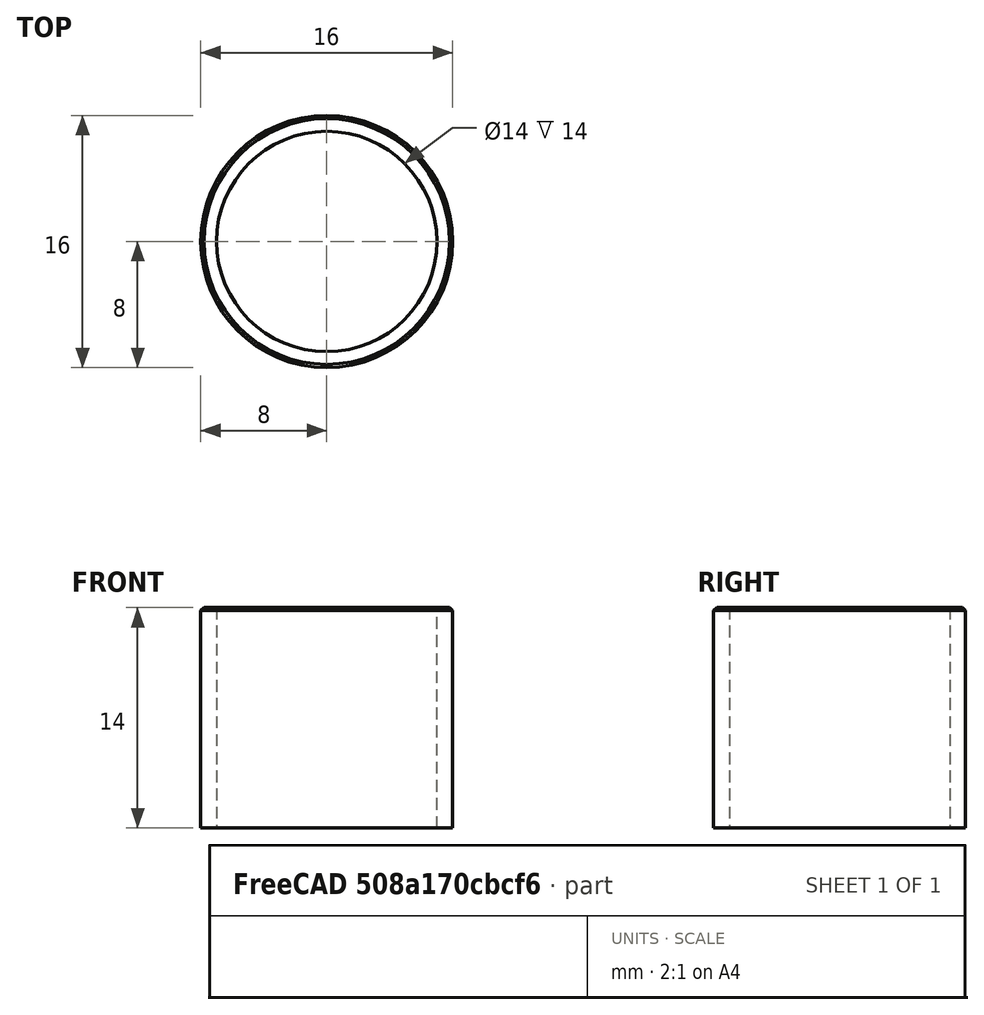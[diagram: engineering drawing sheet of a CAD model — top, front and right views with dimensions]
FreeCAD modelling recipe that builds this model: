
FCSTD DOCUMENT  (FreeCAD 0.19R24276 (Git))
Label: Roller_20_20_in_part_for_Bearing_5x16x5
License: All rights reserved
LicenseURL: http://en.wikipedia.org/wiki/All_rights_reserved
objects: Sketcher::SketchObject×1, PartDesign::Pad×1, PartDesign::Chamfer×1, PartDesign::Body×1
note: 6 computed .brp shape members not serialized (recipe doc carries the construction recipe); baked Part::Feature solids carry a one-line shape summary decoded from their .brp

FEATURE [Sketcher::SketchObject] Sketch
  FullyConstrained = true
  MapMode = 5
  Support = -> [XY_Plane]
  sketch-geometry (2):
    g0: Circle CenterX=0 CenterY=0 CenterZ=0 NormalX=0 NormalY=0 NormalZ=1 AngleXU=0 Radius=8
    g1: Circle CenterX=0 CenterY=0 CenterZ=0 NormalX=0 NormalY=0 NormalZ=1 AngleXU=0 Radius=7
  constraints (4):
    c: Coincident(g0,g-1)
    c: Diameter(g0) = 16
    c: Coincident(g1,g0)
    c: Diameter(g1) = 14
FEATURE [PartDesign::Pad] Pad
  Direction = (1,1,1)
  Length = 14
  Length2 = 100
  Profile = -> Sketch
  Type = 0
FEATURE [PartDesign::Chamfer] Chamfer
  Angle = 45
  Base = -> Pad [Edge3]
  BaseFeature = -> Pad
  ChamferType = 0
  FlipDirection = false
  Size = 0.2
  Size2 = 1
  SupportTransform = false
FEATURE [PartDesign::Body] Body
  Group = -> [Sketch,Pad,Chamfer]
  Origin = -> Origin
  Tip = -> Chamfer
